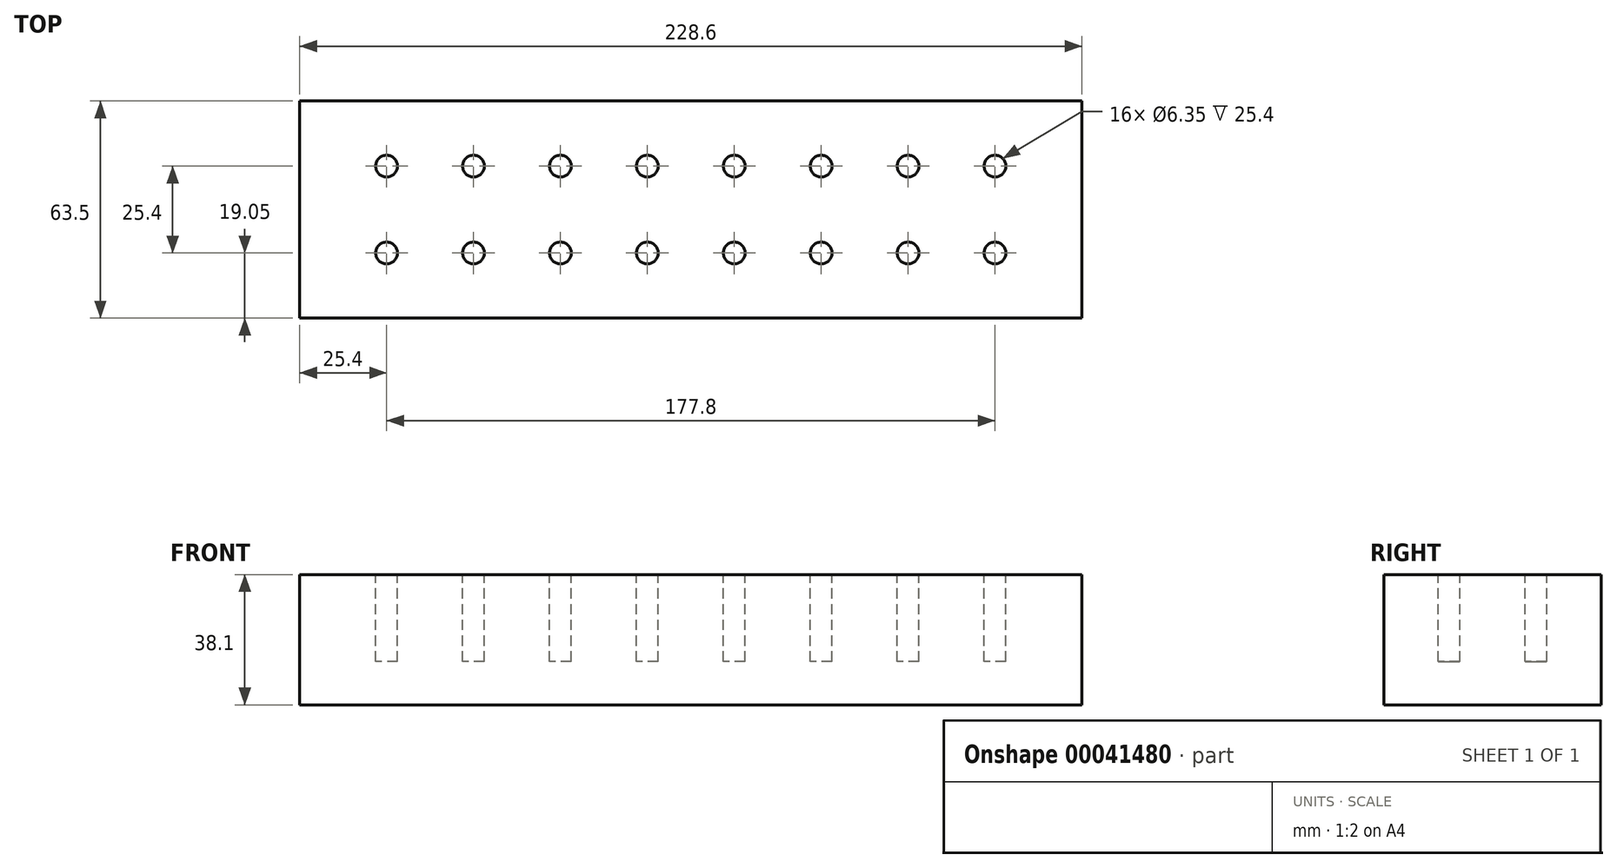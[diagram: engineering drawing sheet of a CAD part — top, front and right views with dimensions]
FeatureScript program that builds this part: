
annotation { "Feature Type Name" : "Feature", "Feature Type Description" : "" }
export const myFeature = defineFeature(function(context is Context, id is Id, definition is map)
    precondition{}
    {
        {
            var Q0;
            Q0=qCreatedBy(makeId("Top.planeOp"),FACE);
            var sketch = newSketch(context, id + "F0", { "sketchPlane" : qUnion([Q0])});
            skLineSegment(sketch, "E0.bottom", {"start": v(-114.3, -31.75) * mm, "end": v(114.3, -31.75) * mm});
            skLineSegment(sketch, "E0.top", {"start": v(-114.3, 31.75) * mm, "end": v(114.3, 31.75) * mm});
            skLineSegment(sketch, "E0.left", {"start": v(-114.3, -31.75) * mm, "end": v(-114.3, 31.75) * mm});
            skLineSegment(sketch, "E0.right", {"start": v(114.3, -31.75) * mm, "end": v(114.3, 31.75) * mm});
            skSolve(sketch);
        }
        {
            var Q0;
            Q0=makeQuery(id+"F0.imprint","IMPRINT",FACE,{"disambiguationData":[TD([[makeQuery(id+"F0.imprint","IMPRINT",EDGE,{"derivedFrom":sQuery(id+"F0.wireOp",EDGE,"E0.bottom")}),1.0]])]});
            extrude(context, id + "F1", {"entities" : qUnion([Q0]), "depth" : 38.1 * mm});
        }
        {
            var Q0;
            Q0=makeQuery(id+"F1.opExtrude","CAP_FACE",FACE,{"disambiguationData":[OSD([sQuery(id+"F0.wireOp",EDGE,"E0.bottom"),sQuery(id+"F0.wireOp",EDGE,"E0.top"),sQuery(id+"F0.wireOp",EDGE,"E0.left"),sQuery(id+"F0.wireOp",EDGE,"E0.right")])],"isStart":false});
            var sketch = newSketch(context, id + "F2", { "sketchPlane" : qUnion([Q0])});
            skCircle(sketch, "E1", {"center": v(-88.9, -12.7) * mm, "radius": 3.18 * mm});
            skCircle(sketch, "E2.0.1.0", {"center": v(-88.9, 12.7) * mm, "radius": 3.18 * mm});
            skCircle(sketch, "E2.1.0.0", {"center": v(-63.5, -12.7) * mm, "radius": 3.18 * mm});
            skCircle(sketch, "E2.1.1.0", {"center": v(-63.5, 12.7) * mm, "radius": 3.18 * mm});
            skCircle(sketch, "E2.2.0.0", {"center": v(-38.1, -12.7) * mm, "radius": 3.18 * mm});
            skCircle(sketch, "E2.2.1.0", {"center": v(-38.1, 12.7) * mm, "radius": 3.18 * mm});
            skCircle(sketch, "E2.3.0.0", {"center": v(-12.7, -12.7) * mm, "radius": 3.18 * mm});
            skCircle(sketch, "E2.3.1.0", {"center": v(-12.7, 12.7) * mm, "radius": 3.18 * mm});
            skCircle(sketch, "E2.4.0.0", {"center": v(12.7, -12.7) * mm, "radius": 3.18 * mm});
            skCircle(sketch, "E2.4.1.0", {"center": v(12.7, 12.7) * mm, "radius": 3.18 * mm});
            skCircle(sketch, "E2.5.0.0", {"center": v(38.1, -12.7) * mm, "radius": 3.18 * mm});
            skCircle(sketch, "E2.5.1.0", {"center": v(38.1, 12.7) * mm, "radius": 3.18 * mm});
            skCircle(sketch, "E2.6.0.0", {"center": v(63.5, -12.7) * mm, "radius": 3.18 * mm});
            skCircle(sketch, "E2.6.1.0", {"center": v(63.5, 12.7) * mm, "radius": 3.18 * mm});
            skCircle(sketch, "E2.7.0.0", {"center": v(88.9, -12.7) * mm, "radius": 3.18 * mm});
            skCircle(sketch, "E2.7.1.0", {"center": v(88.9, 12.7) * mm, "radius": 3.18 * mm});
            skLineSegment(sketch, "E2.direction1", {"start": v(-88.9, -12.7) * mm, "end": v(-63.5, -12.7) * mm, "construction": true});
            skLineSegment(sketch, "E2.direction2", {"start": v(-88.9, -12.7) * mm, "end": v(-88.9, 12.7) * mm, "construction": true});
            skSolve(sketch);
        }
        {
            var Q0;
            Q0 = qSketchRegion(id + "F2", true);
            extrude(context, id + "F3", {"entities" : qUnion([Q0]), "operationType" : NewBodyOperationType.REMOVE, "oppositeDirection" : true, "depth" : 25.4 * mm});
        }
    });
